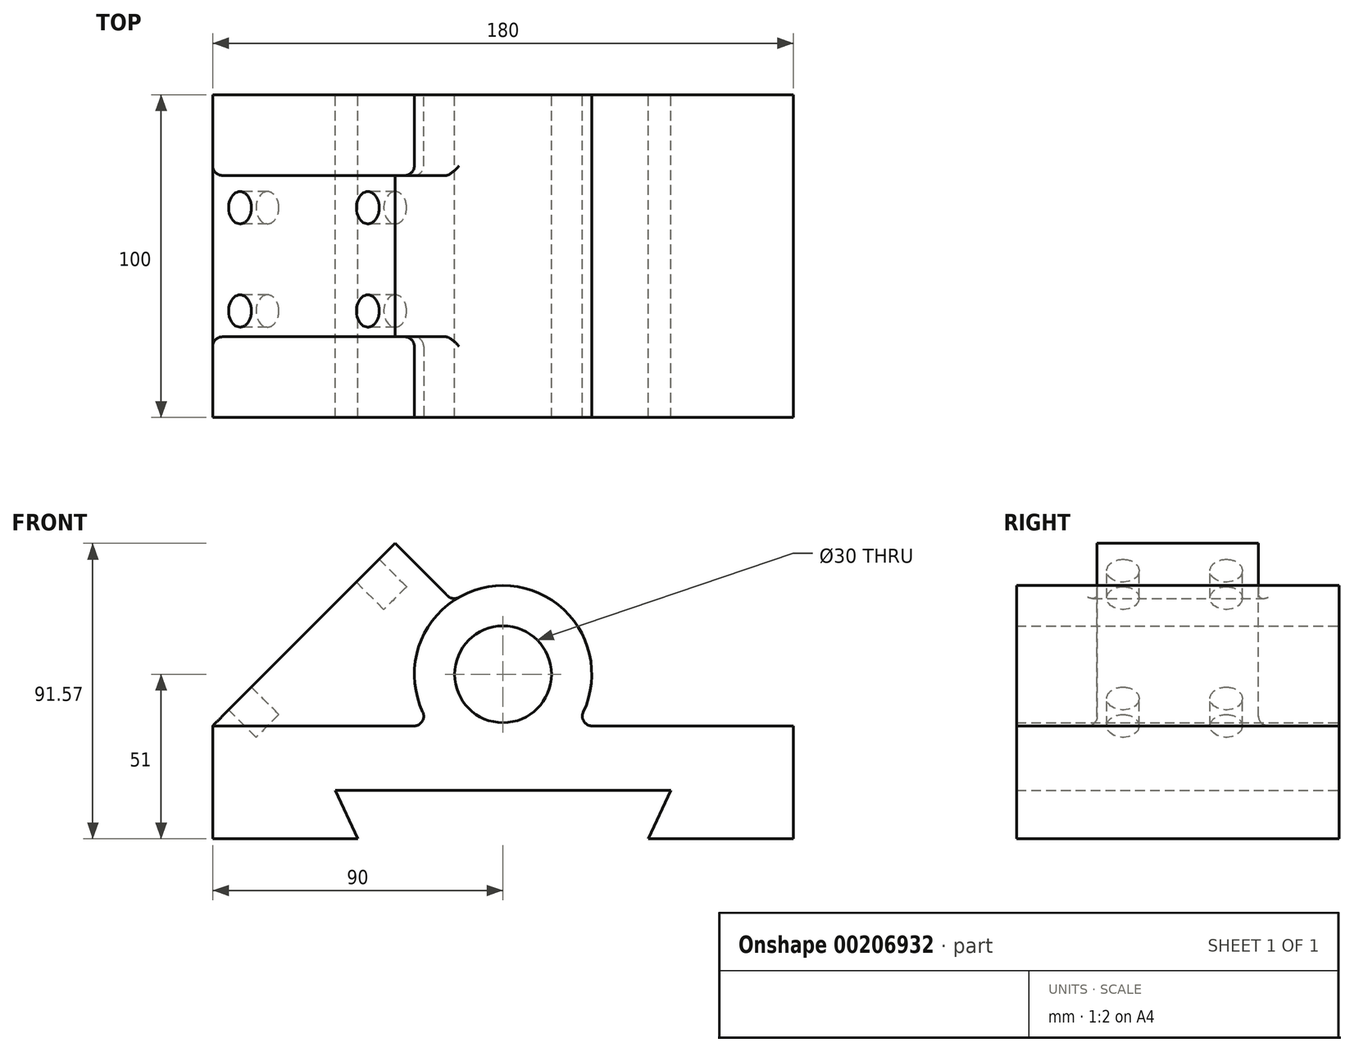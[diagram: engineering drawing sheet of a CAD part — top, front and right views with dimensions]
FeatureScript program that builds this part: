
annotation { "Feature Type Name" : "Feature", "Feature Type Description" : "" }
export const myFeature = defineFeature(function(context is Context, id is Id, definition is map)
    precondition{}
    {
        {
            var Q0;
            Q0=qCreatedBy(makeId("Front.planeOp"),FACE);
            var sketch = newSketch(context, id + "F0", { "sketchPlane" : qUnion([Q0])});
            skCircle(sketch, "E0", {"center": v(0, 0) * mm, "radius": 15 * mm});
            skArc(sketch, "E1", {"start": v(24.88, -11.72) * mm, "mid": v(0, 27.5) * mm, "end": v(-24.88, -11.72) * mm});
            skLineSegment(sketch, "E2", {"start": v(-27.6, -16) * mm, "end": v(-90, -16) * mm});
            skLineSegment(sketch, "E3", {"start": v(-90, -16) * mm, "end": v(-90, -51) * mm});
            skLineSegment(sketch, "E4", {"start": v(-90, -51) * mm, "end": v(-45, -51) * mm});
            skLineSegment(sketch, "E5", {"start": v(-45, -51) * mm, "end": v(-52, -36) * mm});
            skLineSegment(sketch, "E6", {"start": v(-52, -36) * mm, "end": v(52, -36) * mm});
            skLineSegment(sketch, "E7", {"start": v(52, -36) * mm, "end": v(45, -51) * mm});
            skLineSegment(sketch, "E8", {"start": v(45, -51) * mm, "end": v(90, -51) * mm});
            skLineSegment(sketch, "E9", {"start": v(90, -51) * mm, "end": v(90, -16) * mm});
            skLineSegment(sketch, "E10", {"start": v(27.6, -16) * mm, "end": v(90, -16) * mm});
            skLineSegment(sketch, "E11", {"start": v(-90, -16) * mm, "end": v(-33.43, 40.57) * mm});
            skLineSegment(sketch, "E12", {"start": v(-33.43, 40.57) * mm, "end": v(-15.55, 22.68) * mm});
            skPoint(sketch, "E13.visualSharp", {"position": v(22.37, -16) * mm});
            skArc(sketch, "E13.filletArc", {"start": v(24.88, -11.72) * mm, "mid": v(25.06, -14.6) * mm, "end": v(27.6, -16) * mm});
            skPoint(sketch, "E14.visualSharp", {"position": v(-22.37, -16) * mm});
            skArc(sketch, "E14.filletArc", {"start": v(-27.6, -16) * mm, "mid": v(-25.06, -14.6) * mm, "end": v(-24.88, -11.72) * mm});
            skSolve(sketch);
        }
        {
            var Q0;
            {var subQ0=sQuery(id+"F0.wireOp",EDGE,"E2");Q0=makeQuery(id+"F0.imprint","IMPRINT",FACE,{"disambiguationData":[TD([[makeQuery(id+"F0.imprint","IMPRINT",EDGE,{"derivedFrom":subQ0}),-1.0]])]});}
            var Q1;
            Q1=makeQuery(id+"F0.imprint","IMPRINT",FACE,{"disambiguationData":[TD([[makeQuery(id+"F0.imprint","IMPRINT",EDGE,{"derivedFrom":sQuery(id+"F0.wireOp",EDGE,"E0")}),-1.0]])]});
            extrude(context, id + "F1", {"entities" : qUnion([Q0, Q1]), "endBound" : BoundingType.SYMMETRIC, "depth" : 100 * mm});
        }
        {
            var Q0;
            Q0=makeQuery(id+"F1.opExtrude","CAP_FACE",FACE,{"disambiguationData":[OSD([sQuery(id+"F0.wireOp",EDGE,"E0"),sQuery(id+"F0.wireOp",EDGE,"E1"),sQuery(id+"F0.wireOp",EDGE,"E3"),sQuery(id+"F0.wireOp",EDGE,"E4"),sQuery(id+"F0.wireOp",EDGE,"E5"),sQuery(id+"F0.wireOp",EDGE,"E6"),sQuery(id+"F0.wireOp",EDGE,"E7"),sQuery(id+"F0.wireOp",EDGE,"E8"),sQuery(id+"F0.wireOp",EDGE,"E9"),sQuery(id+"F0.wireOp",EDGE,"E10"),sQuery(id+"F0.wireOp",EDGE,"E11"),sQuery(id+"F0.wireOp",EDGE,"E12")])],"isStart":true});
            var sketch = newSketch(context, id + "F2", { "sketchPlane" : qUnion([Q0])});
            skLineSegment(sketch, "E15.0", {"start": v(90, -16) * mm, "end": v(33.43, 40.57) * mm});
            skLineSegment(sketch, "E15.1", {"start": v(33.43, 40.57) * mm, "end": v(15.55, 22.68) * mm});
            skArc(sketch, "E15.2", {"start": v(-24.88, -11.72) * mm, "mid": v(0, 27.5) * mm, "end": v(24.88, -11.72) * mm});
            skLineSegment(sketch, "E15.3", {"start": v(27.6, -16) * mm, "end": v(90, -16) * mm});
            skArc(sketch, "E16.0", {"start": v(27.6, -16) * mm, "mid": v(25.06, -14.6) * mm, "end": v(24.88, -11.72) * mm});
            skSolve(sketch);
        }
        {
            var Q0;
            Q0=makeQuery(id+"F2.imprint","IMPRINT",FACE,{"disambiguationData":[TD([[makeQuery(id+"F2.imprint","IMPRINT",EDGE,{"derivedFrom":sQuery(id+"F2.wireOp",EDGE,"E15.0")}),1.0]])]});
            extrude(context, id + "F3", {"entities" : qUnion([Q0]), "operationType" : NewBodyOperationType.REMOVE, "oppositeDirection" : true, "depth" : 25 * mm});
        }
        {
            var Q0;
            Q0=makeQuery(id+"F1.opExtrude","CAP_FACE",FACE,{"disambiguationData":[OSD([sQuery(id+"F0.wireOp",EDGE,"E0"),sQuery(id+"F0.wireOp",EDGE,"E1"),sQuery(id+"F0.wireOp",EDGE,"E3"),sQuery(id+"F0.wireOp",EDGE,"E4"),sQuery(id+"F0.wireOp",EDGE,"E5"),sQuery(id+"F0.wireOp",EDGE,"E6"),sQuery(id+"F0.wireOp",EDGE,"E7"),sQuery(id+"F0.wireOp",EDGE,"E8"),sQuery(id+"F0.wireOp",EDGE,"E9"),sQuery(id+"F0.wireOp",EDGE,"E10"),sQuery(id+"F0.wireOp",EDGE,"E11"),sQuery(id+"F0.wireOp",EDGE,"E12")])],"isStart":false});
            var sketch = newSketch(context, id + "F4", { "sketchPlane" : qUnion([Q0])});
            skLineSegment(sketch, "E17.0", {"start": v(-27.6, -16) * mm, "end": v(-90, -16) * mm});
            skLineSegment(sketch, "E17.1", {"start": v(-90, -16) * mm, "end": v(-33.43, 40.57) * mm});
            skArc(sketch, "E17.2", {"start": v(24.88, -11.72) * mm, "mid": v(0, 27.5) * mm, "end": v(-24.88, -11.72) * mm});
            skLineSegment(sketch, "E17.3", {"start": v(-33.43, 40.57) * mm, "end": v(-15.55, 22.68) * mm});
            skArc(sketch, "E18.0", {"start": v(-27.6, -16) * mm, "mid": v(-25.06, -14.6) * mm, "end": v(-24.88, -11.72) * mm});
            skSolve(sketch);
        }
        {
            var Q0;
            {var subQ0=sQuery(id+"F4.wireOp",EDGE,"E17.0");Q0=makeQuery(id+"F4.imprint","IMPRINT",FACE,{"disambiguationData":[TD([[makeQuery(id+"F4.imprint","IMPRINT",EDGE,{"derivedFrom":subQ0}),-1.0]])]});}
            extrude(context, id + "F5", {"entities" : qUnion([Q0]), "operationType" : NewBodyOperationType.REMOVE, "oppositeDirection" : true, "depth" : 25 * mm});
        }
        {
            var Q0;
            Q0=makeQuery(id+"F1.opExtrude","SWEPT_FACE",FACE,{"disambiguationData":[OSD([sQuery(id+"F0.wireOp",EDGE,"E11")])]});
            var sketch = newSketch(context, id + "F6", { "sketchPlane" : qUnion([Q0])});
            skCircle(sketch, "E19", {"center": v(-15, -6.95) * mm, "radius": 5 * mm});
            skCircle(sketch, "E20.0.1.0", {"center": v(-15, -62.95) * mm, "radius": 5 * mm});
            skCircle(sketch, "E20.1.0.0", {"center": v(17, -6.95) * mm, "radius": 5 * mm});
            skCircle(sketch, "E20.1.1.0", {"center": v(17, -62.95) * mm, "radius": 5 * mm});
            skLineSegment(sketch, "E20.direction1", {"start": v(-15, -6.95) * mm, "end": v(17, -6.95) * mm, "construction": true});
            skLineSegment(sketch, "E20.direction2", {"start": v(-15, -6.95) * mm, "end": v(-15, -62.95) * mm, "construction": true});
            skSolve(sketch);
        }
        {
            var Q0;
            Q0=makeQuery(id+"F6.imprint","IMPRINT",FACE,{"disambiguationData":[TD([[makeQuery(id+"F6.imprint","IMPRINT",EDGE,{"derivedFrom":sQuery(id+"F6.wireOp",EDGE,"E19")}),1.0]])]});
            var Q1;
            Q1=makeQuery(id+"F6.imprint","IMPRINT",FACE,{"disambiguationData":[TD([[makeQuery(id+"F6.imprint","IMPRINT",EDGE,{"derivedFrom":sQuery(id+"F6.wireOp",EDGE,"E20.0.1.0")}),1.0]])]});
            var Q2;
            Q2=makeQuery(id+"F6.imprint","IMPRINT",FACE,{"disambiguationData":[TD([[makeQuery(id+"F6.imprint","IMPRINT",EDGE,{"derivedFrom":sQuery(id+"F6.wireOp",EDGE,"E20.1.1.0")}),1.0]])]});
            var Q3;
            Q3=makeQuery(id+"F6.imprint","IMPRINT",FACE,{"disambiguationData":[TD([[makeQuery(id+"F6.imprint","IMPRINT",EDGE,{"derivedFrom":sQuery(id+"F6.wireOp",EDGE,"E20.1.0.0")}),1.0]])]});
            extrude(context, id + "F7", {"entities" : qUnion([Q0, Q1, Q2, Q3]), "operationType" : NewBodyOperationType.REMOVE, "oppositeDirection" : true, "depth" : 12 * mm});
        }
        {
            var Q0;
            Q0=makeQuery(id+"F3.boolean.opBoolean","COPY",EDGE,{"derivedFrom":makeQuery(id+"F3.opExtrude","CAP_EDGE",EDGE,{"disambiguationData":[OSD([sQuery(id+"F2.wireOp",EDGE,"E15.3")])],"isStart":false})});
            var Q1;
            Q1=makeQuery(id+"F5.boolean.opBoolean","COPY",EDGE,{"derivedFrom":makeQuery(id+"F5.opExtrude","CAP_EDGE",EDGE,{"disambiguationData":[OSD([sQuery(id+"F4.wireOp",EDGE,"E17.0")])],"isStart":false})});
            var Q2;
            Q2=makeQuery(id+"F1.opExtrude","SWEPT_EDGE",EDGE,{"disambiguationData":[OSD([sQuery(id+"F0.wireOp",EDGE,"E1"),sQuery(id+"F0.wireOp",EDGE,"E12")])]});
            fillet(context, id + "F8", {"entities" : qUnion([Q0, Q1, Q2]), "radius" : 3 * mm, "tangentPropagation" : true, "allowEdgeOverflow" : false});
        }
    });
